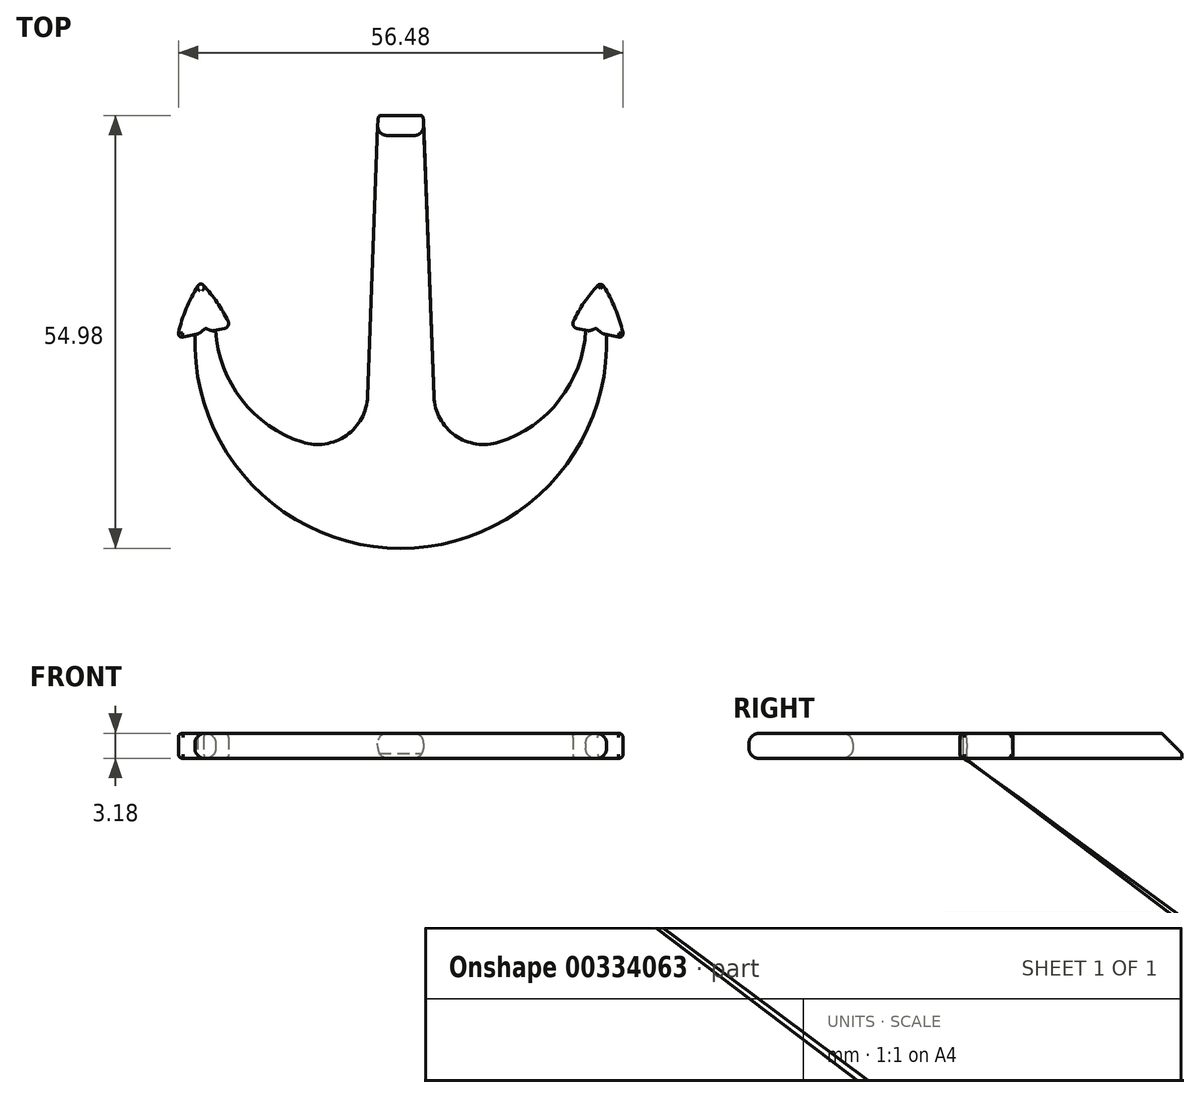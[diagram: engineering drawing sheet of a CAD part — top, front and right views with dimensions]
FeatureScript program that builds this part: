
annotation { "Feature Type Name" : "Feature", "Feature Type Description" : "" }
export const myFeature = defineFeature(function(context is Context, id is Id, definition is map)
    precondition{}
    {
        {
            var Q0;
            Q0=qCreatedBy(makeId("Top.planeOp"),FACE);
            var sketch = newSketch(context, id + "F0", { "sketchPlane" : qUnion([Q0])});
            skArc(sketch, "E0", {"start": v(0, -63.87) * mm, "mid": v(18.84, -55.86) * mm, "end": v(26.13, -36.73) * mm});
            skArc(sketch, "E1", {"start": v(12.5, -50.38) * mm, "mid": v(20.2, -44.98) * mm, "end": v(23.5, -36.18) * mm});
            skLineSegment(sketch, "E2", {"start": v(22.38, -35.94) * mm, "end": v(23.5, -36.18) * mm});
            skArc(sketch, "E3", {"start": v(25.02, -30.5) * mm, "mid": v(23.31, -32.64) * mm, "end": v(21.93, -35.02) * mm});
            skArc(sketch, "E4", {"start": v(28.23, -36.47) * mm, "mid": v(27.25, -33.42) * mm, "end": v(25.78, -30.56) * mm});
            skPoint(sketch, "E5.visualSharp", {"position": v(21.58, -35.77) * mm});
            skArc(sketch, "E5.filletArc", {"start": v(21.93, -35.02) * mm, "mid": v(21.93, -35.6) * mm, "end": v(22.38, -35.94) * mm});
            skPoint(sketch, "E6.visualSharp", {"position": v(28.38, -37.2) * mm});
            skArc(sketch, "E6.filletArc", {"start": v(27.66, -37.05) * mm, "mid": v(28.1, -36.91) * mm, "end": v(28.23, -36.47) * mm});
            skPoint(sketch, "E7.visualSharp", {"position": v(25.45, -30.05) * mm});
            skArc(sketch, "E7.filletArc", {"start": v(25.78, -30.56) * mm, "mid": v(25.42, -30.34) * mm, "end": v(25.02, -30.5) * mm});
            skLineSegment(sketch, "E8.trimOffspring", {"start": v(26.13, -36.73) * mm, "end": v(27.66, -37.05) * mm});
            skArc(sketch, "E9.MirrorCS", {"start": v(-12.5, -50.38) * mm, "mid": v(-20.2, -44.98) * mm, "end": v(-23.5, -36.18) * mm});
            skArc(sketch, "E10.MirrorCS", {"start": v(0, -63.87) * mm, "mid": v(-18.84, -55.86) * mm, "end": v(-26.13, -36.73) * mm});
            skArc(sketch, "E11.MirrorCS", {"start": v(-25.02, -30.5) * mm, "mid": v(-23.31, -32.64) * mm, "end": v(-21.93, -35.02) * mm});
            skArc(sketch, "E12.MirrorCS", {"start": v(-28.23, -36.47) * mm, "mid": v(-27.25, -33.42) * mm, "end": v(-25.78, -30.56) * mm});
            skPoint(sketch, "E13.MirrorP", {"position": v(-25.45, -30.05) * mm});
            skLineSegment(sketch, "E14.MirrorCS", {"start": v(-22.38, -35.94) * mm, "end": v(-23.5, -36.18) * mm});
            skLineSegment(sketch, "E15.MirrorCS", {"start": v(-26.13, -36.73) * mm, "end": v(-27.66, -37.05) * mm});
            skArc(sketch, "E16", {"start": v(-28.23, -36.47) * mm, "mid": v(-28.1, -36.91) * mm, "end": v(-27.66, -37.05) * mm});
            skArc(sketch, "E17", {"start": v(-22.38, -35.94) * mm, "mid": v(-21.93, -35.6) * mm, "end": v(-21.93, -35.02) * mm});
            skArc(sketch, "E18", {"start": v(-25.02, -30.5) * mm, "mid": v(-25.42, -30.3) * mm, "end": v(-25.78, -30.56) * mm});
            skPoint(sketch, "E19.orphan", {"position": v(0, -3.81) * mm});
            skPoint(sketch, "E20.orphan", {"position": v(0, 0) * mm});
            skLineSegment(sketch, "E21.trimOffspring", {"start": v(2.87, -8.9) * mm, "end": v(4.21, -44.57) * mm});
            skLineSegment(sketch, "E22.trimOffspring", {"start": v(-2.87, -8.9) * mm, "end": v(-4.21, -44.57) * mm});
            skPoint(sketch, "E23.visualSharp", {"position": v(4.45, -50.8) * mm});
            skArc(sketch, "E23.filletArc", {"start": v(4.21, -44.57) * mm, "mid": v(6.9, -49.52) * mm, "end": v(12.5, -50.38) * mm});
            skPoint(sketch, "E24.visualSharp", {"position": v(-4.44, -50.8) * mm});
            skArc(sketch, "E24.filletArc", {"start": v(-12.5, -50.38) * mm, "mid": v(-6.9, -49.52) * mm, "end": v(-4.21, -44.57) * mm});
            skPoint(sketch, "E25", {"position": v(0, 9.4) * mm});
            skPoint(sketch, "E26.orphan", {"position": v(-2.78, -6.35) * mm});
            skPoint(sketch, "E27.orphan", {"position": v(2.78, -6.35) * mm});
            skPoint(sketch, "E28", {"position": v(3.17, -3.18) * mm});
            skLineSegment(sketch, "E29.0", {"start": v(-2.87, -8.9) * mm, "end": v(2.87, -8.9) * mm});
            skSolve(sketch);
        }
        {
            var Q0;
            Q0=makeQuery(id+"F0.imprint","IMPRINT",FACE,{"disambiguationData":[TD([[makeQuery(id+"F0.imprint","IMPRINT",EDGE,{"derivedFrom":sQuery(id+"F0.wireOp",EDGE,"E0")}),1.0]])]});
            extrude(context, id + "F1", {"entities" : qUnion([Q0]), "depth" : 3.17 * mm});
        }
        {
            var Q0;
            Q0=makeQuery(id+"F1.opExtrude","CAP_EDGE",EDGE,{"disambiguationData":[OSD([sQuery(id+"F0.wireOp",EDGE,"E4")])],"isStart":false});
            var Q1;
            Q1=makeQuery(id+"F1.opExtrude","CAP_EDGE",EDGE,{"disambiguationData":[OSD([sQuery(id+"F0.wireOp",EDGE,"E4")])],"isStart":true});
            var Q2;
            Q2=makeQuery(id+"F1.opExtrude","CAP_EDGE",EDGE,{"disambiguationData":[OSD([sQuery(id+"F0.wireOp",EDGE,"E11.MirrorCS")])],"isStart":true});
            var Q3;
            Q3=makeQuery(id+"F1.opExtrude","CAP_EDGE",EDGE,{"disambiguationData":[OSD([sQuery(id+"F0.wireOp",EDGE,"E12.MirrorCS")])],"isStart":true});
            var Q4;
            Q4=makeQuery(id+"F1.opExtrude","CAP_EDGE",EDGE,{"disambiguationData":[OSD([sQuery(id+"F0.wireOp",EDGE,"E11.MirrorCS")])],"isStart":false});
            var Q5;
            Q5=makeQuery(id+"F1.opExtrude","CAP_EDGE",EDGE,{"disambiguationData":[OSD([sQuery(id+"F0.wireOp",EDGE,"E12.MirrorCS")])],"isStart":false});
            fillet(context, id + "F2", {"entities" : qUnion([Q0, Q1, Q2, Q3, Q4, Q5]), "radius" : 0.5 * mm, "tangentPropagation" : true, "allowEdgeOverflow" : false});
        }
        {
            var Q0;
            Q0=makeQuery(id+"F1.opExtrude","CAP_EDGE",EDGE,{"disambiguationData":[OSD([sQuery(id+"F0.wireOp",EDGE,"E29.0")])],"isStart":false});
            chamfer(context, id + "F3", {"entities" : qUnion([Q0]), "width" : 2.54 * mm, "tangentPropagation" : true});
        }
        {
            var Q0;
            Q0=makeQuery(id+"F1.opExtrude","CAP_EDGE",EDGE,{"disambiguationData":[OSD([sQuery(id+"F0.wireOp",EDGE,"E21.trimOffspring")])],"isStart":false});
            var Q1;
            Q1=makeQuery(id+"F1.opExtrude","CAP_EDGE",EDGE,{"disambiguationData":[OSD([sQuery(id+"F0.wireOp",EDGE,"E22.trimOffspring")])],"isStart":false});
            var Q2;
            Q2=makeQuery(id+"F1.opExtrude","CAP_EDGE",EDGE,{"disambiguationData":[OSD([sQuery(id+"F0.wireOp",EDGE,"E0"),sQuery(id+"F0.wireOp",EDGE,"E10.MirrorCS")])],"isStart":false});
            var Q3;
            Q3=makeQuery(id+"F1.opExtrude","CAP_EDGE",EDGE,{"disambiguationData":[OSD([sQuery(id+"F0.wireOp",EDGE,"E0"),sQuery(id+"F0.wireOp",EDGE,"E10.MirrorCS")])],"isStart":true});
            var Q4;
            Q4=makeQuery(id+"F1.opExtrude","CAP_EDGE",EDGE,{"disambiguationData":[OSD([sQuery(id+"F0.wireOp",EDGE,"E24.filletArc")])],"isStart":false});
            var Q5;
            Q5=makeQuery(id+"F1.opExtrude","CAP_EDGE",EDGE,{"disambiguationData":[OSD([sQuery(id+"F0.wireOp",EDGE,"E22.trimOffspring")])],"isStart":true});
            var Q6;
            Q6=makeQuery(id+"F1.opExtrude","CAP_EDGE",EDGE,{"disambiguationData":[OSD([sQuery(id+"F0.wireOp",EDGE,"E21.trimOffspring")])],"isStart":true});
            fillet(context, id + "F4", {"entities" : qUnion([Q0, Q1, Q2, Q3, Q4, Q5, Q6]), "radius" : 1.27 * mm, "tangentPropagation" : true, "allowEdgeOverflow" : false});
        }
    });
